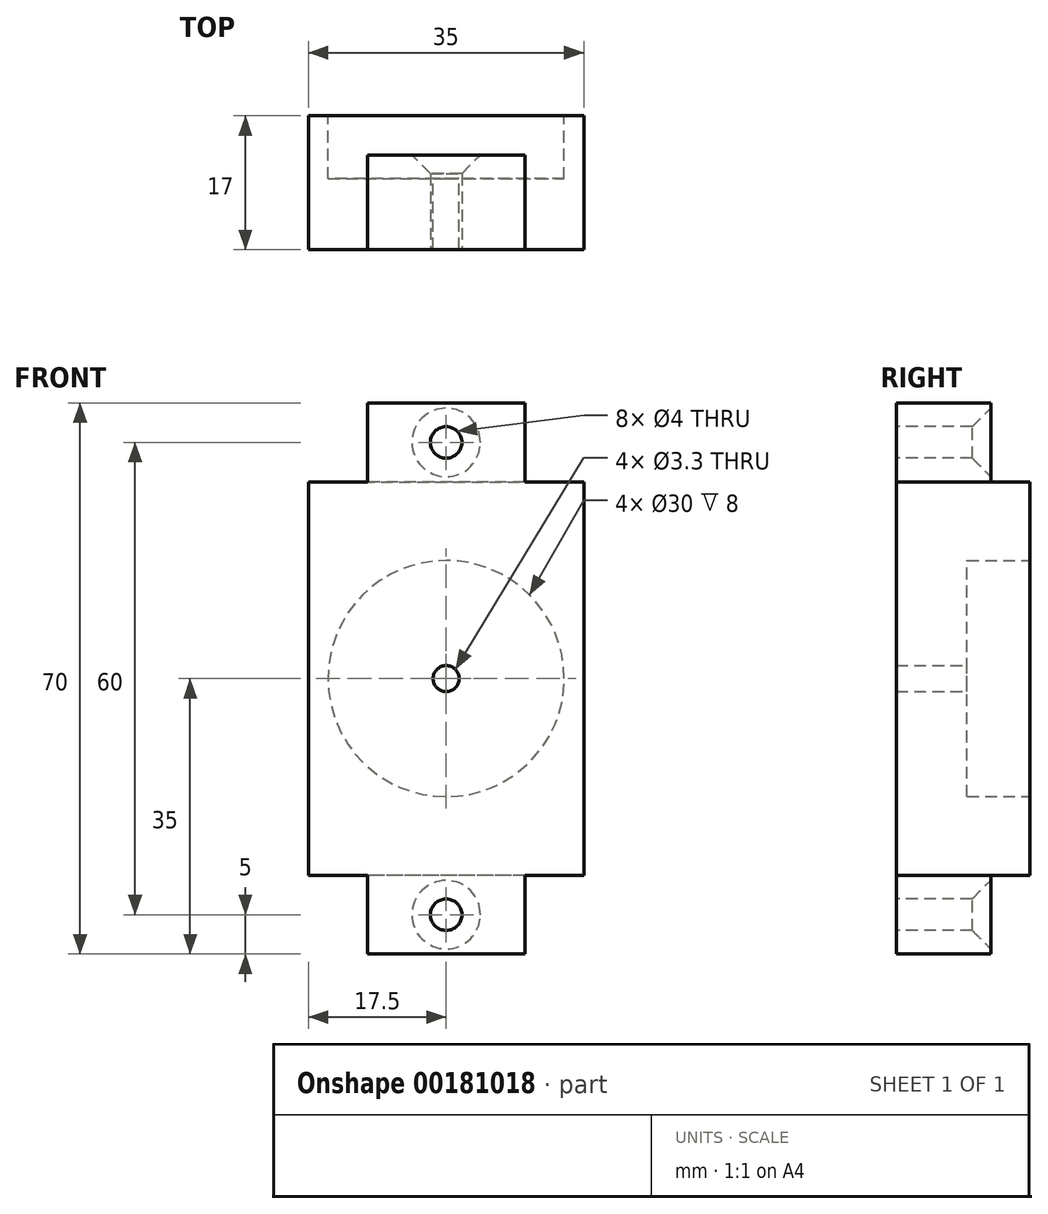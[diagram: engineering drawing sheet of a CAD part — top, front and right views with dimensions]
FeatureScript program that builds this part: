
annotation { "Feature Type Name" : "Feature", "Feature Type Description" : "" }
export const myFeature = defineFeature(function(context is Context, id is Id, definition is map)
    precondition{}
    {
        {
            var Q0;
            Q0=qCreatedBy(makeId("Front.planeOp"),FACE);
            var sketch = newSketch(context, id + "F0", { "sketchPlane" : qUnion([Q0])});
            skCircle(sketch, "E0", {"center": v(0, 0) * mm, "radius": 15 * mm});
            skLineSegment(sketch, "E1", {"start": v(0, 15) * mm, "end": v(0, 25) * mm});
            skLineSegment(sketch, "E2", {"start": v(0, 25) * mm, "end": v(-17.5, 25) * mm});
            skLineSegment(sketch, "E3", {"start": v(-17.5, 25) * mm, "end": v(-17.5, -25) * mm});
            skLineSegment(sketch, "E4", {"start": v(-17.5, -25) * mm, "end": v(0, -25) * mm});
            skLineSegment(sketch, "E5", {"start": v(-10, 25) * mm, "end": v(-10, 35) * mm});
            skLineSegment(sketch, "E6", {"start": v(-10, 35) * mm, "end": v(0, 35) * mm});
            skLineSegment(sketch, "E7.MirrorCS", {"start": v(10, 25) * mm, "end": v(10, 35) * mm});
            skLineSegment(sketch, "E8.MirrorCS", {"start": v(10, 35) * mm, "end": v(0, 35) * mm});
            skLineSegment(sketch, "E9.MirrorCS", {"start": v(0, 25) * mm, "end": v(17.5, 25) * mm});
            skLineSegment(sketch, "E10.MirrorCS", {"start": v(17.5, 25) * mm, "end": v(17.5, -25) * mm});
            skLineSegment(sketch, "E11.MirrorCS", {"start": v(17.5, -25) * mm, "end": v(0, -25) * mm});
            skLineSegment(sketch, "E12", {"start": v(-17.5, 0) * mm, "end": v(-67.5, 0) * mm});
            skPoint(sketch, "E12.endSnap0", {"position": v(-17.5, 0) * mm});
            skLineSegment(sketch, "E13.MirrorCS", {"start": v(10, -35) * mm, "end": v(0, -35) * mm});
            skLineSegment(sketch, "E14.MirrorCS", {"start": v(10, -25) * mm, "end": v(10, -35) * mm});
            skLineSegment(sketch, "E15.MirrorCS", {"start": v(-10, -35) * mm, "end": v(0, -35) * mm});
            skLineSegment(sketch, "E16.MirrorCS", {"start": v(-10, -25) * mm, "end": v(-10, -35) * mm});
            skCircle(sketch, "E17", {"center": v(0, 0) * mm, "radius": 1.65 * mm});
            skSolve(sketch);
        }
        {
            var Q0;
            Q0=makeQuery(id+"F0.imprint","IMPRINT",FACE,{"disambiguationData":[TD([[makeQuery(id+"F0.imprint","IMPRINT",EDGE,{"derivedFrom":sQuery(id+"F0.wireOp",EDGE,"E0")}),-1.0]])]});
            var Q1;
            Q1=makeQuery(id+"F0.imprint","IMPRINT",FACE,{"disambiguationData":[TD([[makeQuery(id+"F0.imprint","IMPRINT",EDGE,{"derivedFrom":sQuery(id+"F0.wireOp",EDGE,"E0")}),1.0]])]});
            var Q2;
            {var subQ0=sQuery(id+"F0.wireOp",EDGE,"E6");Q2=makeQuery(id+"F0.imprint","IMPRINT",FACE,{"disambiguationData":[TD([[makeQuery(id+"F0.imprint","IMPRINT",EDGE,{"derivedFrom":subQ0}),-1.0]])]});}
            var Q3;
            Q3=makeQuery(id+"F0.imprint","IMPRINT",FACE,{"disambiguationData":[TD([[makeQuery(id+"F0.imprint","IMPRINT",EDGE,{"derivedFrom":sQuery(id+"F0.wireOp",EDGE,"E13.MirrorCS")}),-1.0]])]});
            extrude(context, id + "F1", {"entities" : qUnion([Q0, Q1, Q2, Q3]), "offsetDistance" : 25 * mm, "depth" : 17 * mm});
        }
        {
            var Q0;
            Q0=makeQuery(id+"F0.imprint","IMPRINT",FACE,{"disambiguationData":[TD([[makeQuery(id+"F0.imprint","IMPRINT",EDGE,{"derivedFrom":sQuery(id+"F0.wireOp",EDGE,"E0")}),1.0]])]});
            extrude(context, id + "F2", {"entities" : qUnion([Q0]), "operationType" : NewBodyOperationType.REMOVE, "offsetDistance" : 25 * mm, "depth" : 8 * mm});
        }
        {
            var Q0;
            {var subQ0=sQuery(id+"F0.wireOp",EDGE,"E6");Q0=makeQuery(id+"F0.imprint","IMPRINT",FACE,{"disambiguationData":[TD([[makeQuery(id+"F0.imprint","IMPRINT",EDGE,{"derivedFrom":subQ0}),-1.0]])]});}
            var Q1;
            Q1=makeQuery(id+"F0.imprint","IMPRINT",FACE,{"disambiguationData":[TD([[makeQuery(id+"F0.imprint","IMPRINT",EDGE,{"derivedFrom":sQuery(id+"F0.wireOp",EDGE,"E13.MirrorCS")}),-1.0]])]});
            extrude(context, id + "F3", {"entities" : qUnion([Q0, Q1]), "operationType" : NewBodyOperationType.REMOVE, "depth" : 5 * mm});
        }
        {
            var Q0;
            Q0=makeQuery(id+"F3.boolean.opBoolean","COPY",FACE,{"derivedFrom":makeQuery(id+"F3.opExtrude","CAP_FACE",FACE,{"disambiguationData":[OSD([sQuery(id+"F0.wireOp",EDGE,"E2"),sQuery(id+"F0.wireOp",EDGE,"E5"),sQuery(id+"F0.wireOp",EDGE,"E6"),sQuery(id+"F0.wireOp",EDGE,"E7.MirrorCS"),sQuery(id+"F0.wireOp",EDGE,"E8.MirrorCS"),sQuery(id+"F0.wireOp",EDGE,"E9.MirrorCS")])],"isStart":false})});
            var sketch = newSketch(context, id + "F4", { "sketchPlane" : qUnion([Q0])});
            skLineSegment(sketch, "E18", {"start": v(-10, 30) * mm, "end": v(0, 30) * mm});
            skSolve(sketch);
        }
        {
            var Q0;
            Q0=makeQuery(id+"F3.boolean.opBoolean","COPY",FACE,{"derivedFrom":makeQuery(id+"F3.opExtrude","CAP_FACE",FACE,{"disambiguationData":[OSD([sQuery(id+"F0.wireOp",EDGE,"E4"),sQuery(id+"F0.wireOp",EDGE,"E11.MirrorCS"),sQuery(id+"F0.wireOp",EDGE,"E13.MirrorCS"),sQuery(id+"F0.wireOp",EDGE,"E14.MirrorCS"),sQuery(id+"F0.wireOp",EDGE,"E15.MirrorCS"),sQuery(id+"F0.wireOp",EDGE,"E16.MirrorCS")])],"isStart":false})});
            var sketch = newSketch(context, id + "F5", { "sketchPlane" : qUnion([Q0])});
            skLineSegment(sketch, "E19", {"start": v(-10, -30) * mm, "end": v(0, -30) * mm});
            skSolve(sketch);
        }
        {
            var Q0;
            Q0=sQuery(id+"F5.wireOp",VERTEX,"E19.end");
            var Q1;
            Q1=sQuery(id+"F4.wireOp",VERTEX,"E18.end");
            var Q2;
            Q2=makeQuery(id+"F1.opExtrude","SWEPT_BODY",BODY,{"disambiguationData":[OSD([sQuery(id+"F0.wireOp",EDGE,"E2"),sQuery(id+"F0.wireOp",EDGE,"E3"),sQuery(id+"F0.wireOp",EDGE,"E4"),sQuery(id+"F0.wireOp",EDGE,"E5"),sQuery(id+"F0.wireOp",EDGE,"E6"),sQuery(id+"F0.wireOp",EDGE,"E7.MirrorCS"),sQuery(id+"F0.wireOp",EDGE,"E8.MirrorCS"),sQuery(id+"F0.wireOp",EDGE,"E9.MirrorCS"),sQuery(id+"F0.wireOp",EDGE,"E10.MirrorCS"),sQuery(id+"F0.wireOp",EDGE,"E11.MirrorCS"),sQuery(id+"F0.wireOp",EDGE,"E13.MirrorCS"),sQuery(id+"F0.wireOp",EDGE,"E14.MirrorCS"),sQuery(id+"F0.wireOp",EDGE,"E15.MirrorCS"),sQuery(id+"F0.wireOp",EDGE,"E16.MirrorCS"),sQuery(id+"F0.wireOp",EDGE,"E17")])]});
            hole(context, id + "F6", {"style" : HoleStyle.C_SINK, "endStyle" : HoleEndStyle.THROUGH, "holeDiameter" : 4 * mm, "cSinkDiameter" : 8.7 * mm, "cSinkAngle" : 90 * degree, "locations" : qUnion([Q0, Q1]), "scope" : qUnion([Q2]), "isTappedThrough" : true, "startStyle" : HoleStartStyle.PART});
        }
    });
